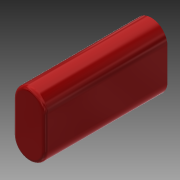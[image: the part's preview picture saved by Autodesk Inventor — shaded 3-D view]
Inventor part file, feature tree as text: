
AUTODESK INVENTOR PART (.ipt)
format: ipt  version: 2018 (Build 220112000, 112)  size: 96,768 bytes
history: native  units: mm (DEFAULTED — no unit token found)
features: extrude x1, fillet x1, sketch x1, reference x1
ambient origin geometry x8: Origin, YZ Plane, XZ Plane, XY Plane, X Axis, Y Axis, Z Axis, Center Point
bodies: Solid1 (feature_tree)
feature tree (4):
  extrude  "Extrusion1"  Depth=0.381mm
  fillet  "Fillet1"  [1 undecoded]
  sketch  "Sketch1"  dims[d0=12.7mm d1=0.0mm d2=0.381mm]
  reference  "Reference1"
note: 1 required parameter value undecoded (feature->parameter linkage not recoverable at this tier; creation-order binding heuristic only, values carry confidence <= 0.55)
